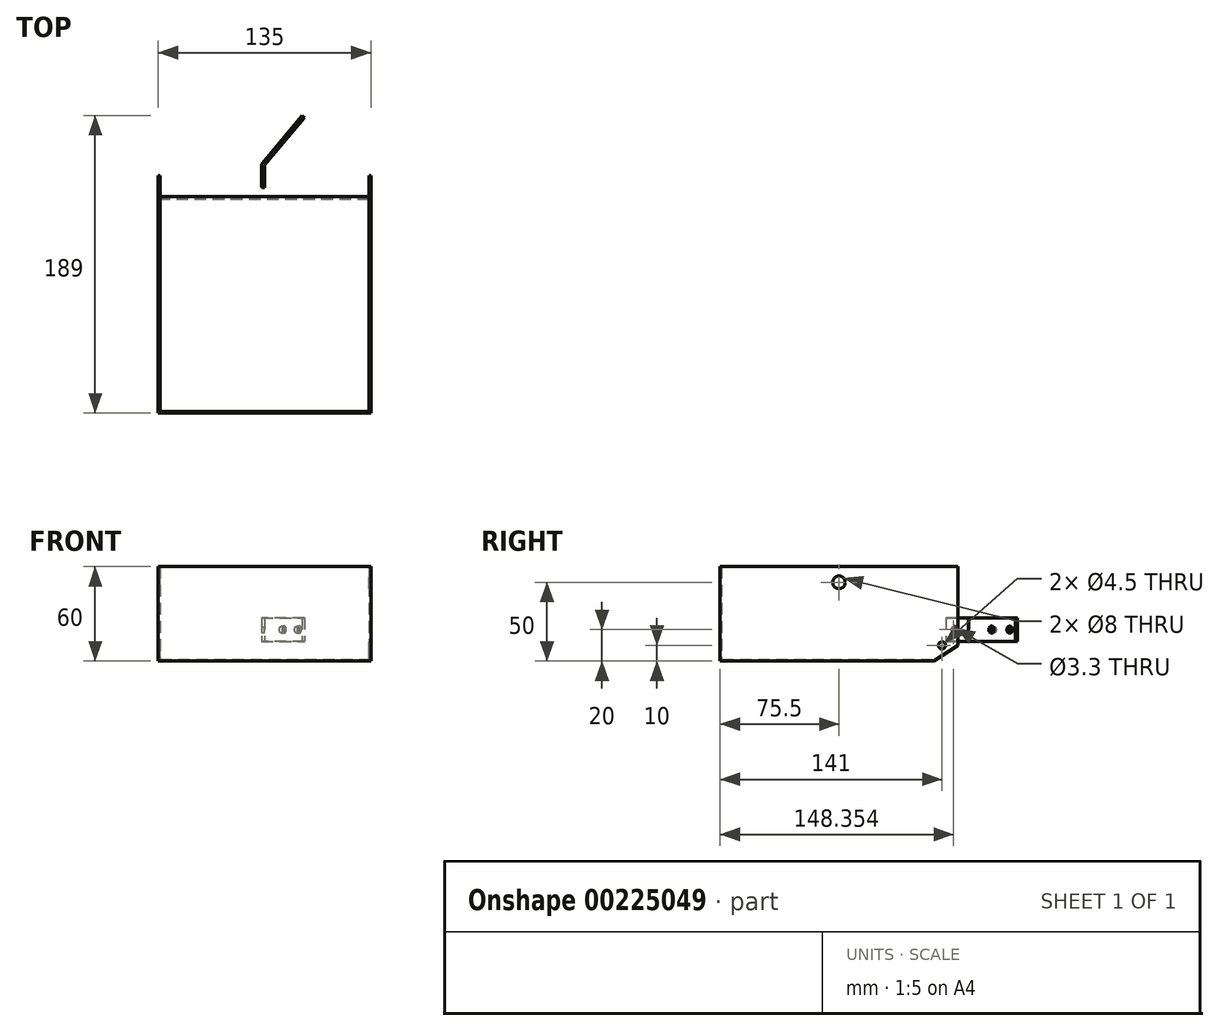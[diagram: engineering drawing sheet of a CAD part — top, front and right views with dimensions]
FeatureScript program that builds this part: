
annotation { "Feature Type Name" : "Feature", "Feature Type Description" : "" }
export const myFeature = defineFeature(function(context is Context, id is Id, definition is map)
    precondition{}
    {
        {
            var Q0;
            Q0=qCreatedBy(makeId("Front.planeOp"),FACE);
            var sketch = newSketch(context, id + "F0", { "sketchPlane" : qUnion([Q0])});
            skLineSegment(sketch, "E0.top", {"start": v(67.5, -20) * mm, "end": v(-67.5, -20) * mm});
            skLineSegment(sketch, "E0.left", {"start": v(67.5, 40) * mm, "end": v(67.5, -20) * mm});
            skLineSegment(sketch, "E0.right", {"start": v(-67.5, 40) * mm, "end": v(-67.5, -20) * mm});
            skLineSegment(sketch, "E1.top", {"start": v(66.5, -19) * mm, "end": v(-66.5, -19) * mm});
            skLineSegment(sketch, "E1.left", {"start": v(66.5, 40) * mm, "end": v(66.5, -19) * mm});
            skLineSegment(sketch, "E1.right", {"start": v(-66.5, 40) * mm, "end": v(-66.5, -19) * mm});
            skLineSegment(sketch, "E2", {"start": v(67.5, 40) * mm, "end": v(66.5, 40) * mm});
            skLineSegment(sketch, "E3", {"start": v(-66.5, 40) * mm, "end": v(-67.5, 40) * mm});
            skSolve(sketch);
        }
        {
            var Q0;
            Q0=qSketchRegion(id+"F0",true);
            extrude(context, id + "F1", {"entities" : qUnion([Q0]), "depth" : 150 * mm});
        }
        {
            var Q0;
            Q0=makeQuery(id+"F1.opExtrude","CAP_FACE",FACE,{"disambiguationData":[OSD([sQuery(id+"F0.wireOp",EDGE,"E0.top"),sQuery(id+"F0.wireOp",EDGE,"E0.left"),sQuery(id+"F0.wireOp",EDGE,"E0.right"),sQuery(id+"F0.wireOp",EDGE,"E1.top"),sQuery(id+"F0.wireOp",EDGE,"E1.left"),sQuery(id+"F0.wireOp",EDGE,"E1.right"),sQuery(id+"F0.wireOp",EDGE,"E2"),sQuery(id+"F0.wireOp",EDGE,"E3")])],"isStart":false});
            var sketch = newSketch(context, id + "F2", { "sketchPlane" : qUnion([Q0])});
            skLineSegment(sketch, "E4.bottom", {"start": v(-67.5, 40) * mm, "end": v(67.5, 40) * mm});
            skLineSegment(sketch, "E4.top", {"start": v(-67.5, -20) * mm, "end": v(67.5, -20) * mm});
            skLineSegment(sketch, "E4.left", {"start": v(-67.5, 40) * mm, "end": v(-67.5, -20) * mm});
            skLineSegment(sketch, "E4.right", {"start": v(67.5, 40) * mm, "end": v(67.5, -20) * mm});
            skSolve(sketch);
        }
        {
            var Q0;
            Q0=qSketchRegion(id+"F2",true);
            extrude(context, id + "F3", {"entities" : qUnion([Q0]), "operationType" : NewBodyOperationType.ADD, "depth" : 1 * mm});
        }
        {
            var Q0;
            Q0=makeQuery(id+"F3.boolean.opBoolean","MERGE",FACE,{"derivedFrom":[makeQuery(id+"F1.opExtrude","SWEPT_FACE",FACE,{"disambiguationData":[OSD([sQuery(id+"F0.wireOp",EDGE,"E0.right")])]}),makeQuery(id+"F3.opExtrude","SWEPT_FACE",FACE,{"disambiguationData":[OSD([sQuery(id+"F2.wireOp",EDGE,"E4.left")])]})]});
            var sketch = newSketch(context, id + "F4", { "sketchPlane" : qUnion([Q0])});
            skPoint(sketch, "E5", {"position": v(10, -10) * mm});
            skPoint(sketch, "E5.positionSnap0", {"position": v(0, 10) * mm});
            skSolve(sketch);
        }
        {
            var Q0;
            Q0=sQuery(id+"F4.wireOp",VERTEX,"E5");
            var Q1;
            Q1=makeQuery(id+"F1.opExtrude","SWEPT_BODY",BODY,{"disambiguationData":[OSD([sQuery(id+"F0.wireOp",EDGE,"E0.top"),sQuery(id+"F0.wireOp",EDGE,"E0.left"),sQuery(id+"F0.wireOp",EDGE,"E0.right"),sQuery(id+"F0.wireOp",EDGE,"E1.top"),sQuery(id+"F0.wireOp",EDGE,"E1.left"),sQuery(id+"F0.wireOp",EDGE,"E1.right"),sQuery(id+"F0.wireOp",EDGE,"E2"),sQuery(id+"F0.wireOp",EDGE,"E3")])]});
            hole(context, id + "F5", {"style" : HoleStyle.SIMPLE, "endStyle" : HoleEndStyle.THROUGH, "holeDiameter" : 4.5 * mm, "locations" : qUnion([Q0]), "scope" : qUnion([Q1]), "tappedDepth" : 12 * mm, "tapClearance" : 3});
        }
        {
            var Q0;
            Q0=makeQuery(id+"F3.boolean.opBoolean","MERGE",FACE,{"derivedFrom":[makeQuery(id+"F1.opExtrude","SWEPT_FACE",FACE,{"disambiguationData":[OSD([sQuery(id+"F0.wireOp",EDGE,"E0.right")])]}),makeQuery(id+"F3.opExtrude","SWEPT_FACE",FACE,{"disambiguationData":[OSD([sQuery(id+"F2.wireOp",EDGE,"E4.left")])]})]});
            var sketch = newSketch(context, id + "F6", { "sketchPlane" : qUnion([Q0])});
            skPoint(sketch, "E6", {"position": v(75.5, 30) * mm});
            skPoint(sketch, "E6.positionSnap0", {"position": v(75.5, 40) * mm});
            skSolve(sketch);
        }
        {
            var Q0;
            Q0=sQuery(id+"F6.wireOp",VERTEX,"E6");
            var Q1;
            Q1=makeQuery(id+"F1.opExtrude","SWEPT_BODY",BODY,{"disambiguationData":[OSD([sQuery(id+"F0.wireOp",EDGE,"E0.top"),sQuery(id+"F0.wireOp",EDGE,"E0.left"),sQuery(id+"F0.wireOp",EDGE,"E0.right"),sQuery(id+"F0.wireOp",EDGE,"E1.top"),sQuery(id+"F0.wireOp",EDGE,"E1.left"),sQuery(id+"F0.wireOp",EDGE,"E1.right"),sQuery(id+"F0.wireOp",EDGE,"E2"),sQuery(id+"F0.wireOp",EDGE,"E3")])]});
            hole(context, id + "F7", {"style" : HoleStyle.SIMPLE, "endStyle" : HoleEndStyle.THROUGH, "holeDiameter" : 8 * mm, "locations" : qUnion([Q0]), "scope" : qUnion([Q1]), "isTappedThrough" : true});
        }
        {
            var Q0;
            Q0=qCreatedBy(makeId("Top.planeOp"),FACE);
            var sketch = newSketch(context, id + "F8", { "sketchPlane" : qUnion([Q0])});
            skLineSegment(sketch, "E7", {"start": v(-2, -7.65) * mm, "end": v(-2, 7.35) * mm});
            skLineSegment(sketch, "E8", {"start": v(-2, 7.35) * mm, "end": v(23.71, 38) * mm});
            skLineSegment(sketch, "E9", {"start": v(23.71, 38) * mm, "end": v(25.24, 36.71) * mm});
            skLineSegment(sketch, "E10", {"start": v(25.24, 36.71) * mm, "end": v(0, 6.63) * mm});
            skLineSegment(sketch, "E11", {"start": v(0, 6.63) * mm, "end": v(0, -7.65) * mm});
            skLineSegment(sketch, "E12", {"start": v(0, -7.65) * mm, "end": v(-2, -7.65) * mm});
            skSolve(sketch);
        }
        {
            var Q0;
            Q0 = qSketchRegion(id + "F8", true);
            extrude(context, id + "F9", {"entities" : qUnion([Q0]), "endBound" : BoundingType.SYMMETRIC, "depth" : 15 * mm});
        }
        {
            var Q0;
            Q0=makeQuery(id+"F9.opExtrude","SWEPT_FACE",FACE,{"disambiguationData":[OSD([sQuery(id+"F8.wireOp",EDGE,"E11")])]});
            var sketch = newSketch(context, id + "F10", { "sketchPlane" : qUnion([Q0])});
            skPoint(sketch, "E13", {"position": v(-2.65, 0) * mm});
            skSolve(sketch);
        }
        {
            var Q0;
            Q0=sQuery(id+"F10.wireOp",VERTEX,"E13");
            var Q1;
            Q1=makeQuery(id+"F9.opExtrude","SWEPT_BODY",BODY,{"disambiguationData":[OSD([sQuery(id+"F8.wireOp",EDGE,"E7"),sQuery(id+"F8.wireOp",EDGE,"E8"),sQuery(id+"F8.wireOp",EDGE,"E9"),sQuery(id+"F8.wireOp",EDGE,"E10"),sQuery(id+"F8.wireOp",EDGE,"E11"),sQuery(id+"F8.wireOp",EDGE,"E12")])]});
            hole(context, id + "F11", {"style" : HoleStyle.SIMPLE, "endStyle" : HoleEndStyle.THROUGH, "standardTappedOrClearance" : lookupTablePath({ "standard" : "ISO", "engagement" : "75%", "pitch" : "0.7 mm", "size" : "M4", "type" : "Tapped" }), "standardBlindInLast" : lookupTablePath({ "standard" : "ISO", "engagement" : "75%", "pitch" : "0.7 mm", "size" : "M4", "type" : "Tapped" }), "holeDiameter" : 3.3 * mm, "showTappedDepth" : true, "tappedDepth" : 12 * mm, "tapClearance" : 3, "locations" : qUnion([Q0]), "scope" : qUnion([Q1]), "majorDiameter" : 4 * mm});
        }
        {
            var Q0;
            Q0=makeQuery(id+"F9.opExtrude","SWEPT_FACE",FACE,{"disambiguationData":[OSD([sQuery(id+"F8.wireOp",EDGE,"E10")])]});
            var sketch = newSketch(context, id + "F12", { "sketchPlane" : qUnion([Q0])});
            skPoint(sketch, "E14", {"position": v(39.35, 0) * mm});
            skPoint(sketch, "E14.positionSnap0", {"position": v(44.35, 0) * mm});
            skPoint(sketch, "E15", {"position": v(24.35, 0) * mm});
            skSolve(sketch);
        }
        {
            var Q0;
            Q0=sQuery(id+"F12.wireOp",VERTEX,"E15");
            var Q1;
            Q1=sQuery(id+"F12.wireOp",VERTEX,"E14");
            var Q2;
            Q2=makeQuery(id+"F9.opExtrude","SWEPT_BODY",BODY,{"disambiguationData":[OSD([sQuery(id+"F8.wireOp",EDGE,"E7"),sQuery(id+"F8.wireOp",EDGE,"E8"),sQuery(id+"F8.wireOp",EDGE,"E9"),sQuery(id+"F8.wireOp",EDGE,"E10"),sQuery(id+"F8.wireOp",EDGE,"E11"),sQuery(id+"F8.wireOp",EDGE,"E12")])]});
            hole(context, id + "F13", {"style" : HoleStyle.SIMPLE, "endStyle" : HoleEndStyle.THROUGH, "standardTappedOrClearance" : lookupTablePath({ "standard" : "ISO", "fit" : "Normal", "size" : "M4", "type" : "Clearance" }), "standardBlindInLast" : lookupTablePath({ "fit" : "Standard", "standard" : "ISO", "size" : "M4", "type" : "Clearance" }), "holeDiameter" : 4.4 * mm, "tappedDepth" : 12 * mm, "tapClearance" : 3, "locations" : qUnion([Q0, Q1]), "scope" : qUnion([Q2])});
        }
        {
            var Q0;
            Q0=makeQuery(id+"F3.boolean.opBoolean","MERGE",FACE,{"derivedFrom":[makeQuery(id+"F1.opExtrude","SWEPT_FACE",FACE,{"disambiguationData":[OSD([sQuery(id+"F0.wireOp",EDGE,"E0.left")])]}),makeQuery(id+"F3.opExtrude","SWEPT_FACE",FACE,{"disambiguationData":[OSD([sQuery(id+"F2.wireOp",EDGE,"E4.right")])]})]});
            var sketch = newSketch(context, id + "F14", { "sketchPlane" : qUnion([Q0])});
            skLineSegment(sketch, "E16", {"start": v(-15, -20) * mm, "end": v(0, -10) * mm});
            skLineSegment(sketch, "E17", {"start": v(0, -10) * mm, "end": v(0, -20) * mm});
            skLineSegment(sketch, "E18", {"start": v(0, -20) * mm, "end": v(-15, -20) * mm});
            skSolve(sketch);
        }
        {
            var Q0;
            Q0 = qSketchRegion(id + "F14", true);
            extrude(context, id + "F15", {"entities" : qUnion([Q0]), "operationType" : NewBodyOperationType.REMOVE, "oppositeDirection" : true, "depth" : 140 * mm});
        }
    });
